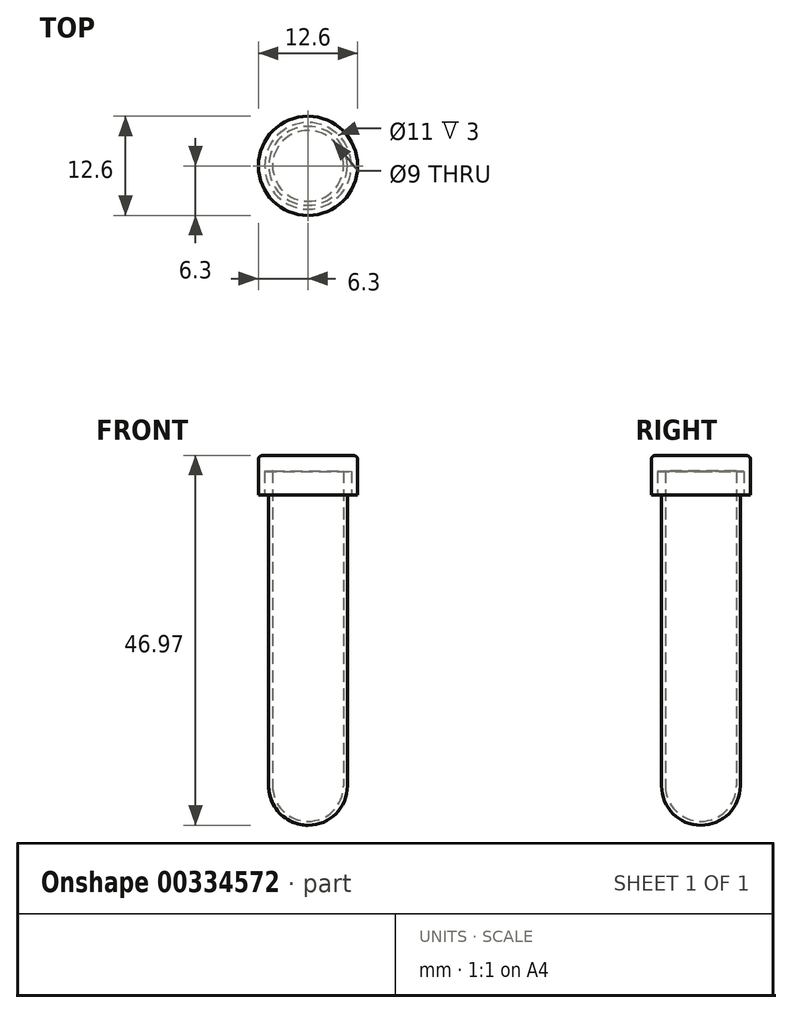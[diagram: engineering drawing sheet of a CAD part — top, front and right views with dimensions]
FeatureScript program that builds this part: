
annotation { "Feature Type Name" : "Feature", "Feature Type Description" : "" }
export const myFeature = defineFeature(function(context is Context, id is Id, definition is map)
    precondition{}
    {
        {
            var Q0;
            Q0=qCreatedBy(makeId("Front.planeOp"),FACE);
            var sketch = newSketch(context, id + "F0", { "sketchPlane" : qUnion([Q0])});
            skLineSegment(sketch, "E0", {"start": v(-5, -0.47) * mm, "end": v(-5, -37.47) * mm});
            skLineSegment(sketch, "E1", {"start": v(0, -42.47) * mm, "end": v(0, -42.47) * mm});
            skLineSegment(sketch, "E2.0", {"start": v(-4.5, 2.5) * mm, "end": v(-4.5, -37.47) * mm});
            skPoint(sketch, "E3.visualSharp", {"position": v(-4.5, -41.97) * mm});
            skArc(sketch, "E3.filletArc", {"start": v(-4.5, -37.47) * mm, "mid": v(-3.18, -40.65) * mm, "end": v(0, -41.97) * mm});
            skPoint(sketch, "E4.visualSharp", {"position": v(-5, -42.47) * mm});
            skArc(sketch, "E4.filletArc", {"start": v(-5, -37.47) * mm, "mid": v(-3.54, -41) * mm, "end": v(0, -42.47) * mm});
            skLineSegment(sketch, "E5", {"start": v(-5.5, 2.5) * mm, "end": v(-5.5, 0) * mm});
            skPoint(sketch, "E6.orphan", {"position": v(-5, 2.53) * mm});
            skLineSegment(sketch, "E7", {"start": v(-5, -0.47) * mm, "end": v(-5.5, -0.47) * mm});
            skLineSegment(sketch, "E8", {"start": v(-5.5, -0.47) * mm, "end": v(-5.5, 0) * mm});
            skPoint(sketch, "E9.orphan", {"position": v(-6.43, 2.5) * mm});
            skLineSegment(sketch, "E10", {"start": v(0, -41.97) * mm, "end": v(0, -42.47) * mm});
            skLineSegment(sketch, "E11", {"start": v(0, -46.13) * mm, "end": v(0, 19.61) * mm, "construction": true});
            skLineSegment(sketch, "E12", {"start": v(-5.5, 2.5) * mm, "end": v(-4.5, 2.5) * mm});
            skPoint(sketch, "E13.orphan", {"position": v(1.52, 2.53) * mm});
            skSolve(sketch);
        }
        {
            var Q0;
            Q0 = qSketchRegion(id + "F0", true);
            var Q1;
            Q1=sQuery(id+"F0.wireOp",EDGE,"E11");
            revolve(context, id + "F1", {"entities" : qUnion([Q0]), "axis" : qUnion([Q1]), "revolveType" : RevolveType.FULL});
        }
        {
            var Q0;
            Q0=qCreatedBy(makeId("Front.planeOp"),FACE);
            var sketch = newSketch(context, id + "F2", { "sketchPlane" : qUnion([Q0])});
            skLineSegment(sketch, "E14", {"start": v(0, 4.5) * mm, "end": v(-6.3, 4.5) * mm});
            skLineSegment(sketch, "E15", {"start": v(-6.3, 4.5) * mm, "end": v(-6.3, -0.5) * mm});
            skLineSegment(sketch, "E16", {"start": v(-6.3, -0.5) * mm, "end": v(-5.5, -0.5) * mm});
            skLineSegment(sketch, "E17", {"start": v(-5.5, -0.5) * mm, "end": v(-5.5, 2.5) * mm});
            skLineSegment(sketch, "E18", {"start": v(-5.5, 2.5) * mm, "end": v(0, 2.5) * mm});
            skLineSegment(sketch, "E19", {"start": v(0, 2.5) * mm, "end": v(0, 4.5) * mm});
            skLineSegment(sketch, "E20", {"start": v(0, 0) * mm, "end": v(0, 4.2) * mm, "construction": true});
            skLineSegment(sketch, "E21", {"start": v(0, 4.5) * mm, "end": v(0, 2.5) * mm});
            skSolve(sketch);
        }
        {
            var Q0;
            Q0=makeQuery(id+"F2.imprint","IMPRINT",FACE,{"disambiguationData":[TD([[makeQuery(id+"F2.imprint","IMPRINT",EDGE,{"derivedFrom":sQuery(id+"F2.wireOp",EDGE,"E14")}),1.0]])]});
            var Q1;
            Q1=sQuery(id+"F2.wireOp",EDGE,"E20");
            revolve(context, id + "F3", {"entities" : qUnion([Q0]), "axis" : qUnion([Q1]), "revolveType" : RevolveType.FULL});
        }
        {
            var Q0;
            Q0=makeQuery(id+"F3.opRevolve","SWEPT_EDGE",EDGE,{"disambiguationData":[OSD([sQuery(id+"F2.wireOp",EDGE,"E14"),sQuery(id+"F2.wireOp",EDGE,"E15")])]});
            fillet(context, id + "F4", {"entities" : qUnion([Q0]), "radius" : 0.5 * mm, "tangentPropagation" : true, "allowEdgeOverflow" : false});
        }
    });
